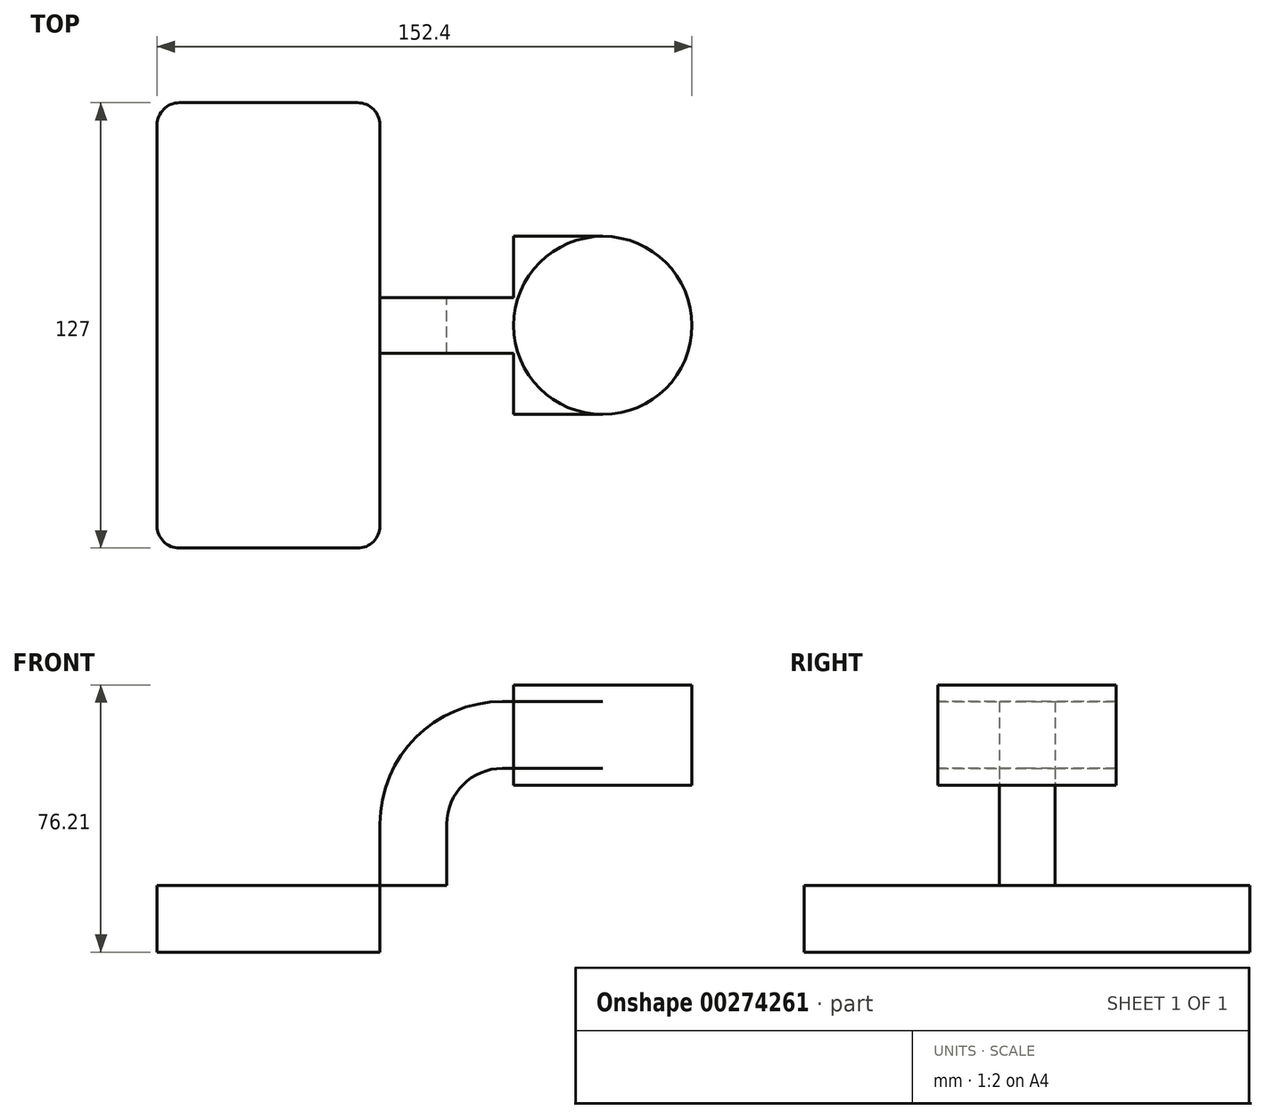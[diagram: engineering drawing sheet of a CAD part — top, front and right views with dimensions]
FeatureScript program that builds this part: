
annotation { "Feature Type Name" : "Feature", "Feature Type Description" : "" }
export const myFeature = defineFeature(function(context is Context, id is Id, definition is map)
    precondition{}
    {
        {
            var Q0;
            Q0=qCreatedBy(makeId("Front.planeOp"),FACE);
            var sketch = newSketch(context, id + "F0", { "sketchPlane" : qUnion([Q0])});
            skLineSegment(sketch, "E0.bottom", {"start": v(41.28, 9.53) * mm, "end": v(-41.28, 9.52) * mm});
            skLineSegment(sketch, "E0.top", {"start": v(41.28, -9.52) * mm, "end": v(-41.28, -9.53) * mm});
            skLineSegment(sketch, "E0.left", {"start": v(41.28, 9.53) * mm, "end": v(41.28, -9.52) * mm});
            skLineSegment(sketch, "E0.right", {"start": v(-41.28, 9.52) * mm, "end": v(-41.28, -9.53) * mm});
            skPoint(sketch, "E0.middle", {"position": v(0, 0) * mm});
            skLineSegment(sketch, "E1.bottom", {"start": v(111.12, 66.68) * mm, "end": v(60.32, 66.68) * mm});
            skLineSegment(sketch, "E1.top", {"start": v(111.12, 38.1) * mm, "end": v(60.33, 38.1) * mm});
            skLineSegment(sketch, "E1.left", {"start": v(111.12, 66.68) * mm, "end": v(111.12, 38.1) * mm});
            skLineSegment(sketch, "E1.right", {"start": v(60.32, 66.68) * mm, "end": v(60.33, 38.1) * mm});
            skPoint(sketch, "E1.middle", {"position": v(85.72, 52.39) * mm});
            skLineSegment(sketch, "E2", {"start": v(41.28, -9.52) * mm, "end": v(41.28, 27) * mm});
            skArc(sketch, "E3", {"start": v(41.27, 27) * mm, "mid": v(45.92, 38.23) * mm, "end": v(57.15, 42.88) * mm});
            skLineSegment(sketch, "E4", {"start": v(57.15, 42.88) * mm, "end": v(85.72, 42.88) * mm});
            skLineSegment(sketch, "E5.0", {"start": v(57.15, 61.93) * mm, "end": v(85.72, 61.93) * mm});
            skArc(sketch, "E5.1", {"start": v(22.23, 27) * mm, "mid": v(32.45, 51.7) * mm, "end": v(57.15, 61.93) * mm});
            skLineSegment(sketch, "E5.2", {"start": v(22.22, -9.52) * mm, "end": v(22.22, 27) * mm});
            skFitSpline(sketch, "E6", {"points": [v(-41.28, 9.52) * mm, v(57.15, 61.93) * mm], "startDerivative": vector(14.93, 115.47) * mm, "endDerivative": vector(107.03, -11.52) * mm});
            skPoint(sketch, "E7", {"position": v(85.72, 38.1) * mm});
            skLineSegment(sketch, "E8", {"start": v(85.72, 38.1) * mm, "end": v(85.72, 66.68) * mm});
            skSolve(sketch);
        }
        {
            var Q0;
            {var subQ0=sQuery(id+"F0.wireOp",EDGE,"E0.right");Q0=makeQuery(id+"F0.imprint","IMPRINT",FACE,{"disambiguationData":[TD([[makeQuery(id+"F0.imprint","IMPRINT",EDGE,{"derivedFrom":subQ0}),1.0]])]});}
            extrude(context, id + "F1", {"entities" : qUnion([Q0]), "endBound" : BoundingType.SYMMETRIC, "depth" : 127 * mm});
        }
        {
            var Q0;
            {var subQ0=sQuery(id+"F0.wireOp",EDGE,"E3");Q0=makeQuery(id+"F0.imprint","IMPRINT",FACE,{"disambiguationData":[TD([[makeQuery(id+"F0.imprint","IMPRINT",EDGE,{"derivedFrom":subQ0}),1.0]])]});}
            var Q1;
            {var subQ0=sQuery(id+"F0.wireOp",EDGE,"E5.0");var subQ1=sQuery(id+"F0.wireOp",EDGE,"E1.right");var subQ2=makeQuery(id+"F0.imprint","INTERSECT",VERTEX,{"derivedFrom":[subQ1,subQ0]});Q1=makeQuery(id+"F0.imprint","IMPRINT",FACE,{"disambiguationData":[TD([[makeQuery(id+"F0.imprint","IMPRINT",EDGE,{"disambiguationData":[TD([[subQ2,-1.0]])],"derivedFrom":subQ1}),1.0]])]});}
            extrude(context, id + "F2", {"entities" : qUnion([Q0, Q1]), "endBound" : BoundingType.SYMMETRIC, "depth" : 50.8 * mm});
        }
        {
            var Q0;
            {var subQ4=sQuery(id+"F0.wireOp",EDGE,"E5.1");Q0=makeQuery(id+"F0.imprint","IMPRINT",FACE,{"disambiguationData":[TD([[makeQuery(id+"F0.imprint","IMPRINT",EDGE,{"derivedFrom":subQ4}),1.0]])]});}
            extrude(context, id + "F3", {"entities" : qUnion([Q0]), "endBound" : BoundingType.SYMMETRIC, "depth" : 15.88 * mm});
        }
        {
            var Q0;
            {var subQ4=sQuery(id+"F0.wireOp",EDGE,"E1.left");Q0=makeQuery(id+"F0.imprint","IMPRINT",FACE,{"disambiguationData":[TD([[makeQuery(id+"F0.imprint","IMPRINT",EDGE,{"derivedFrom":subQ4}),-1.0]])]});}
            var Q1;
            Q1=sQuery(id+"F0.wireOp",EDGE,"E8");
            revolve(context, id + "F4", {"operationType" : NewBodyOperationType.ADD, "entities" : qUnion([Q0]), "axis" : qUnion([Q1]), "revolveType" : RevolveType.FULL});
        }
        {
            var Q0;
            Q0=makeQuery(id+"F1.opExtrude","CAP_EDGE",EDGE,{"disambiguationData":[OSD([sQuery(id+"F0.wireOp",EDGE,"E0.right")])],"isStart":false});
            var Q1;
            Q1=makeQuery(id+"F1.opExtrude","CAP_EDGE",EDGE,{"disambiguationData":[OSD([sQuery(id+"F0.wireOp",EDGE,"E5.2")])],"isStart":false});
            var Q2;
            Q2=makeQuery(id+"F1.opExtrude","CAP_EDGE",EDGE,{"disambiguationData":[OSD([sQuery(id+"F0.wireOp",EDGE,"E0.right")])],"isStart":true});
            var Q3;
            Q3=makeQuery(id+"F1.opExtrude","CAP_EDGE",EDGE,{"disambiguationData":[OSD([sQuery(id+"F0.wireOp",EDGE,"E5.2")])],"isStart":true});
            fillet(context, id + "F5", {"entities" : qUnion([Q0, Q1, Q2, Q3]), "radius" : 6.35 * mm, "tangentPropagation" : true, "allowEdgeOverflow" : false});
        }
    });
